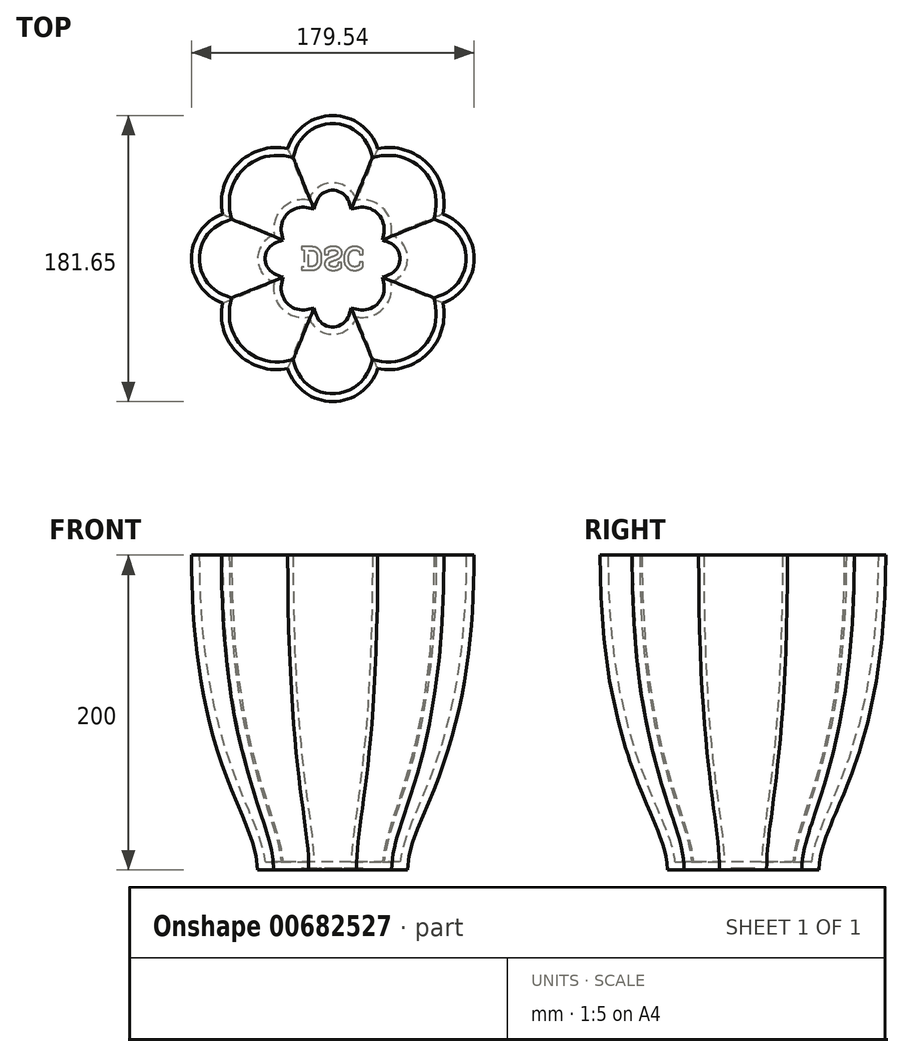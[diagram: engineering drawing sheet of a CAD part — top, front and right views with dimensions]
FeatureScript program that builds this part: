
annotation { "Feature Type Name" : "Feature", "Feature Type Description" : "" }
export const myFeature = defineFeature(function(context is Context, id is Id, definition is map)
    precondition{}
    {
        {
            var Q0;
            Q0=qCreatedBy(makeId("Top.planeOp"),FACE);
            var sketch = newSketch(context, id + "F0", { "sketchPlane" : qUnion([Q0])});
            skArc(sketch, "E0.0.1.0", {"start": v(-70, -28.19) * mm, "mid": v(-60.45, -60.14) * mm, "end": v(-28.58, -69.94) * mm});
            skArc(sketch, "E0.1.0.0", {"start": v(70, 28.21) * mm, "mid": v(60.45, 60.16) * mm, "end": v(28.58, 69.96) * mm});
            skArc(sketch, "E1.trimOffspring", {"start": v(-70, 28.21) * mm, "mid": v(-89.77, 0.01) * mm, "end": v(-70, -28.19) * mm});
            skArc(sketch, "E2.trimOffspring", {"start": v(28.58, 69.96) * mm, "mid": v(0, 90.84) * mm, "end": v(-28.58, 69.96) * mm});
            skArc(sketch, "E3.trimOffspring", {"start": v(70, -28.19) * mm, "mid": v(89.77, 0.01) * mm, "end": v(70, 28.21) * mm});
            skArc(sketch, "E4.trimOffspring", {"start": v(-28.58, -69.94) * mm, "mid": v(0, -90.81) * mm, "end": v(28.58, -69.94) * mm});
            skArc(sketch, "E5.trimOffspring", {"start": v(-28.58, 69.96) * mm, "mid": v(-60.45, 60.16) * mm, "end": v(-70, 28.21) * mm});
            skArc(sketch, "E6.trimOffspring", {"start": v(28.58, -69.94) * mm, "mid": v(60.45, -60.14) * mm, "end": v(70, -28.19) * mm});
            skSolve(sketch);
        }
        {
            var Q0;
            Q0=qCreatedBy(makeId("Top.planeOp"),FACE);
            cPlane(context, id + "F1", {"entities" : qUnion([Q0]), "cplaneType" : CPlaneType.OFFSET, "offset" : 200 * mm, "oppositeDirection" : true, "width" : 150 * mm, "height" : 150 * mm});
        }
        {
            var Q0;
            Q0=qCreatedBy(id+"F1.planeOp",FACE);
            var sketch = newSketch(context, id + "F2", { "sketchPlane" : qUnion([Q0])});
            skArc(sketch, "E7.0.1.0", {"start": v(-37.17, -14.94) * mm, "mid": v(-32.11, -31.87) * mm, "end": v(-15.22, -37.06) * mm});
            skArc(sketch, "E7.1.0.0", {"start": v(37.03, 14.96) * mm, "mid": v(31.97, 31.9) * mm, "end": v(15.08, 37.09) * mm});
            skArc(sketch, "E8.trimOffspring", {"start": v(-37.17, 14.96) * mm, "mid": v(-47.65, 0.01) * mm, "end": v(-37.17, -14.94) * mm});
            skArc(sketch, "E9.trimOffspring", {"start": v(15.08, 37.09) * mm, "mid": v(-0.07, 48.15) * mm, "end": v(-15.22, 37.09) * mm});
            skArc(sketch, "E10.trimOffspring", {"start": v(37.03, -14.94) * mm, "mid": v(47.5, 0.01) * mm, "end": v(37.03, 14.96) * mm});
            skArc(sketch, "E11.trimOffspring", {"start": v(-15.22, -37.06) * mm, "mid": v(-0.07, -48.13) * mm, "end": v(15.08, -37.06) * mm});
            skArc(sketch, "E12.trimOffspring", {"start": v(-15.22, 37.09) * mm, "mid": v(-32.11, 31.9) * mm, "end": v(-37.17, 14.96) * mm});
            skArc(sketch, "E13.trimOffspring", {"start": v(15.08, -37.06) * mm, "mid": v(31.97, -31.87) * mm, "end": v(37.03, -14.94) * mm});
            skSolve(sketch);
        }
        {
            var Q0;
            Q0=makeQuery(id+"F0.imprint","IMPRINT",FACE,{"disambiguationData":[TD([[makeQuery(id+"F0.imprint","IMPRINT",EDGE,{"derivedFrom":sQuery(id+"F0.wireOp",EDGE,"E0.0.1.0")}),1.0]])]});
            var Q1;
            Q1=makeQuery(id+"F2.imprint","IMPRINT",FACE,{"disambiguationData":[TD([[makeQuery(id+"F2.imprint","IMPRINT",EDGE,{"derivedFrom":sQuery(id+"F2.wireOp",EDGE,"E7.0.1.0")}),1.0]])]});
            loft(context, id + "F3", {"startCondition" : LoftEndDerivativeType.NORMAL_TO_PROFILE, "startMagnitude" : 2, "endCondition" : LoftEndDerivativeType.NORMAL_TO_PROFILE, "endMagnitude" : 0.5, "sheetProfilesArray" : [{ "sheetProfileEntities" : qUnion([Q0]) }, { "sheetProfileEntities" : qUnion([Q1]) }]});
        }
        {
            var Q0;
            Q0=makeQuery(id+"F3.opLoft","CAP_FACE",FACE,{"disambiguationData":[OSD([makeQuery(id+"F0.imprint","IMPRINT",FACE,{"disambiguationData":[TD([[makeQuery(id+"F0.imprint","IMPRINT",EDGE,{"derivedFrom":sQuery(id+"F0.wireOp",EDGE,"E0.0.1.0")}),1.0]])]})])],"isStart":true});
            shell(context, id + "F4", {"entities" : qUnion([Q0]), "thickness" : 5 * mm});
        }
        {
            var Q0;
            Q0=makeQuery(id+"F3.opLoft","CAP_FACE",FACE,{"disambiguationData":[OSD([makeQuery(id+"F2.imprint","IMPRINT",FACE,{"disambiguationData":[TD([[makeQuery(id+"F2.imprint","IMPRINT",EDGE,{"derivedFrom":sQuery(id+"F2.wireOp",EDGE,"E7.0.1.0")}),1.0]])]})])],"isStart":true});
            var sketch = newSketch(context, id + "F5", { "sketchPlane" : qUnion([Q0])});
            skText(sketch, "E14", { "text": "DSC", "fontName": "RobotoSlab-Bold.ttf"});
            const initialGuessF5  = {"E14": [-0.02048, -0.0075, 1, 0, 0.015]};
            skSetInitialGuess(sketch, initialGuessF5);
            skSolve(sketch);
        }
        {
            var Q0;
            Q0 = qSketchRegion(id + "F5", true);
            extrude(context, id + "F6", {"entities" : qUnion([Q0]), "operationType" : NewBodyOperationType.REMOVE, "oppositeDirection" : true, "depth" : 1 * mm, "offsetDistance" : 25 * mm});
        }
    });
